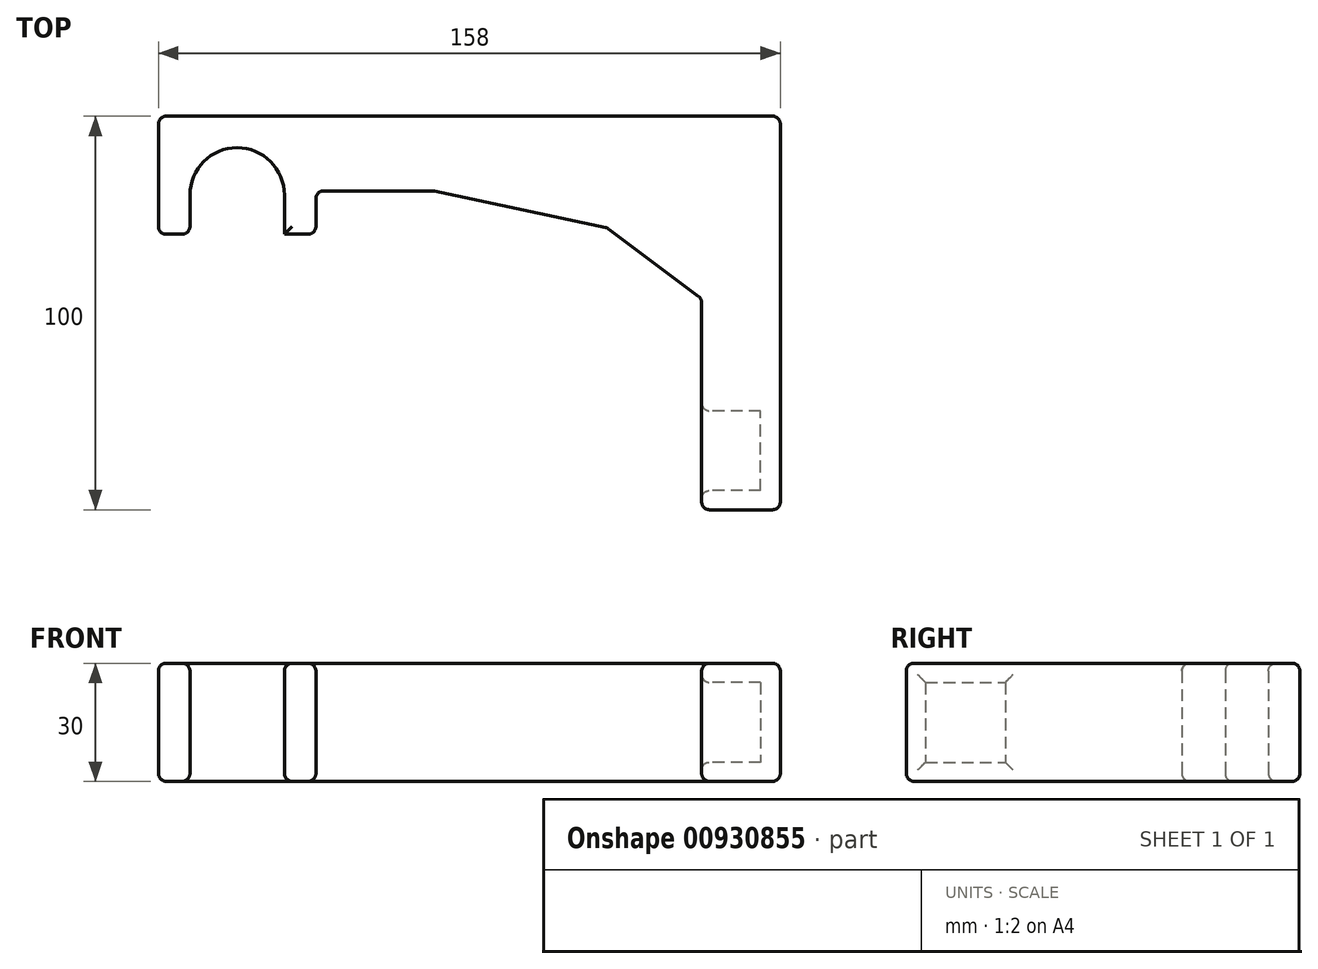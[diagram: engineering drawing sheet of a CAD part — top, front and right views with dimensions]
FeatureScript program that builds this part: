
annotation { "Feature Type Name" : "Feature", "Feature Type Description" : "" }
export const myFeature = defineFeature(function(context is Context, id is Id, definition is map)
    precondition{}
    {
        {
            var Q0;
            Q0=qCreatedBy(makeId("Top.planeOp"),FACE);
            var sketch = newSketch(context, id + "F0", { "sketchPlane" : qUnion([Q0])});
            skCircle(sketch, "E0", {"center": v(0, 5) * mm, "radius": 12 * mm});
            skLineSegment(sketch, "E1", {"start": v(-20, 25) * mm, "end": v(138, 25) * mm});
            skLineSegment(sketch, "E2", {"start": v(138, 25) * mm, "end": v(138, -15) * mm});
            skLineSegment(sketch, "E3", {"start": v(138, -15) * mm, "end": v(138, -75) * mm});
            skLineSegment(sketch, "E4", {"start": v(138, -75) * mm, "end": v(118, -75) * mm});
            skLineSegment(sketch, "E5", {"start": v(50, 5) * mm, "end": v(50, 6) * mm, "construction": true});
            skLineSegment(sketch, "E6", {"start": v(50, 6) * mm, "end": v(94.02, -3.36) * mm});
            skLineSegment(sketch, "E7", {"start": v(118, -75) * mm, "end": v(118, -21.38) * mm});
            skLineSegment(sketch, "E8", {"start": v(94.02, -3.36) * mm, "end": v(118, -21.38) * mm});
            skLineSegment(sketch, "E9", {"start": v(-12, 25) * mm, "end": v(-12, -5) * mm});
            skLineSegment(sketch, "E10.MirrorCS", {"start": v(12, 25) * mm, "end": v(12, -5) * mm});
            skLineSegment(sketch, "E11", {"start": v(-20, 25) * mm, "end": v(-20, -5) * mm});
            skLineSegment(sketch, "E12", {"start": v(-20, -5) * mm, "end": v(-12, -5) * mm});
            skLineSegment(sketch, "E13", {"start": v(12, -5) * mm, "end": v(20, -5) * mm});
            skLineSegment(sketch, "E14", {"start": v(50, 6) * mm, "end": v(20, 6) * mm});
            skLineSegment(sketch, "E15", {"start": v(20, 6) * mm, "end": v(20, -5) * mm});
            skLineSegment(sketch, "E16", {"start": v(0, 5) * mm, "end": v(118.79, 5) * mm, "construction": true});
            skSolve(sketch);
        }
        {
            var Q0;
            Q0=makeQuery(id+"F0.imprint","IMPRINT",FACE,{"disambiguationData":[TD([[makeQuery(id+"F0.imprint","IMPRINT",EDGE,{"derivedFrom":sQuery(id+"F0.wireOp",EDGE,"718Cw2XN-Loyv-s3oq-BlH3-nW312tGR8hBX.bottom")}),1.0]])]});
            var Q1;
            Q1=makeQuery(id+"F0.imprint","IMPRINT",FACE,{"disambiguationData":[TD([[makeQuery(id+"F0.imprint","IMPRINT",EDGE,{"derivedFrom":sQuery(id+"F0.wireOp",EDGE,"E1")}),-1.0]])]});
            var Q2;
            {var subQ3=sQuery(id+"F0.wireOp",EDGE,"zue7M12d-nwCh-ULH3-EO4g-m9Mkl6G7epCl");Q2=makeQuery(id+"F0.imprint","IMPRINT",FACE,{"disambiguationData":[TD([[makeQuery(id+"F0.imprint","IMPRINT",EDGE,{"derivedFrom":subQ3}),1.0]])]});}
            var Q3;
            {var subQ1=sQuery(id+"F0.wireOp",EDGE,"E3");Q3=makeQuery(id+"F0.imprint","IMPRINT",FACE,{"disambiguationData":[TD([[makeQuery(id+"F0.imprint","IMPRINT",EDGE,{"derivedFrom":subQ1}),-1.0]])]});}
            var Q4;
            {var subQ3=sQuery(id+"F0.wireOp",EDGE,"usQBu0dE-cOZz-AhfG-xYus-OKftIOVNqgJ2");Q4=makeQuery(id+"F0.imprint","IMPRINT",FACE,{"disambiguationData":[TD([[makeQuery(id+"F0.imprint","IMPRINT",EDGE,{"derivedFrom":subQ3}),-1.0]])]});}
            var Q5;
            {var subQ0=sQuery(id+"F0.wireOp",EDGE,"E11");Q5=makeQuery(id+"F0.imprint","IMPRINT",FACE,{"disambiguationData":[TD([[makeQuery(id+"F0.imprint","IMPRINT",EDGE,{"derivedFrom":subQ0}),1.0]])]});}
            extrude(context, id + "F1", {"entities" : qUnion([Q0, Q1, Q2, Q3, Q4, Q5]), "depth" : 30 * mm, "offsetDistance" : 25 * mm});
        }
        {
            var Q0;
            Q0=makeQuery(id+"F1.opExtrude","SWEPT_FACE",FACE,{"disambiguationData":[OSD([sQuery(id+"F0.wireOp",EDGE,"E7")])]});
            var sketch = newSketch(context, id + "F2", { "sketchPlane" : qUnion([Q0])});
            skLineSegment(sketch, "E17", {"start": v(75, 15) * mm, "end": v(21.38, 15) * mm, "construction": true});
            skPoint(sketch, "E18", {"position": v(60, 15) * mm});
            skLineSegment(sketch, "E19.bottom", {"start": v(70.12, 25.12) * mm, "end": v(49.87, 25.12) * mm});
            skLineSegment(sketch, "E19.top", {"start": v(70.12, 4.87) * mm, "end": v(49.87, 4.87) * mm});
            skLineSegment(sketch, "E19.left", {"start": v(70.12, 25.12) * mm, "end": v(70.12, 4.87) * mm});
            skLineSegment(sketch, "E19.right", {"start": v(49.87, 25.12) * mm, "end": v(49.87, 4.87) * mm});
            skSolve(sketch);
        }
        {
            var Q0;
            Q0=makeQuery(id+"F2.imprint","IMPRINT",FACE,{"disambiguationData":[TD([[makeQuery(id+"F2.imprint","IMPRINT",EDGE,{"derivedFrom":sQuery(id+"F2.wireOp",EDGE,"E19.bottom")}),1.0]])]});
            extrude(context, id + "F3", {"entities" : qUnion([Q0]), "operationType" : NewBodyOperationType.REMOVE, "oppositeDirection" : true, "depth" : 15 * mm, "offsetDistance" : 25 * mm});
        }
        {
            var Q0;
            Q0=makeQuery(id+"F1.opExtrude","SWEPT_FACE",FACE,{"disambiguationData":[OSD([sQuery(id+"F0.wireOp",EDGE,"E15")])]});
            var Q1;
            Q1=makeQuery(id+"F1.opExtrude","SWEPT_FACE",FACE,{"disambiguationData":[OSD([sQuery(id+"F0.wireOp",EDGE,"E14")])]});
            var Q2;
            Q2=makeQuery(id+"F1.opExtrude","SWEPT_FACE",FACE,{"disambiguationData":[OSD([sQuery(id+"F0.wireOp",EDGE,"E8")])]});
            var Q3;
            Q3=makeQuery(id+"F1.opExtrude","SWEPT_FACE",FACE,{"disambiguationData":[OSD([sQuery(id+"F0.wireOp",EDGE,"E7")])]});
            var Q4;
            Q4=makeQuery(id+"F1.opExtrude","SWEPT_FACE",FACE,{"disambiguationData":[OSD([sQuery(id+"F0.wireOp",EDGE,"E4")])]});
            var Q5;
            Q5=makeQuery(id+"F1.opExtrude","CAP_FACE",FACE,{"disambiguationData":[OSD([sQuery(id+"F0.wireOp",EDGE,"E0"),sQuery(id+"F0.wireOp",EDGE,"E1"),sQuery(id+"F0.wireOp",EDGE,"E2"),sQuery(id+"F0.wireOp",EDGE,"E3"),sQuery(id+"F0.wireOp",EDGE,"E4"),sQuery(id+"F0.wireOp",EDGE,"E6"),sQuery(id+"F0.wireOp",EDGE,"E7"),sQuery(id+"F0.wireOp",EDGE,"E8"),sQuery(id+"F0.wireOp",EDGE,"E9"),sQuery(id+"F0.wireOp",EDGE,"E10.MirrorCS"),sQuery(id+"F0.wireOp",EDGE,"E11"),sQuery(id+"F0.wireOp",EDGE,"E12"),sQuery(id+"F0.wireOp",EDGE,"E13"),sQuery(id+"F0.wireOp",EDGE,"E14"),sQuery(id+"F0.wireOp",EDGE,"E15")])],"isStart":false});
            var Q6;
            Q6=makeQuery(id+"F1.opExtrude","CAP_FACE",FACE,{"disambiguationData":[OSD([sQuery(id+"F0.wireOp",EDGE,"E0"),sQuery(id+"F0.wireOp",EDGE,"E1"),sQuery(id+"F0.wireOp",EDGE,"E2"),sQuery(id+"F0.wireOp",EDGE,"E3"),sQuery(id+"F0.wireOp",EDGE,"E4"),sQuery(id+"F0.wireOp",EDGE,"E6"),sQuery(id+"F0.wireOp",EDGE,"E7"),sQuery(id+"F0.wireOp",EDGE,"E8"),sQuery(id+"F0.wireOp",EDGE,"E9"),sQuery(id+"F0.wireOp",EDGE,"E10.MirrorCS"),sQuery(id+"F0.wireOp",EDGE,"E11"),sQuery(id+"F0.wireOp",EDGE,"E12"),sQuery(id+"F0.wireOp",EDGE,"E13"),sQuery(id+"F0.wireOp",EDGE,"E14"),sQuery(id+"F0.wireOp",EDGE,"E15")])],"isStart":true});
            var Q7;
            Q7=makeQuery(id+"F1.opExtrude","SWEPT_FACE",FACE,{"disambiguationData":[OSD([sQuery(id+"F0.wireOp",EDGE,"E12")])]});
            var Q8;
            Q8=makeQuery(id+"F1.opExtrude","SWEPT_FACE",FACE,{"disambiguationData":[OSD([sQuery(id+"F0.wireOp",EDGE,"E1")])]});
            fillet(context, id + "F4", {"entities" : qUnion([Q0, Q1, Q2, Q3, Q4, Q5, Q6, Q7, Q8]), "radius" : 2 * mm, "tangentPropagation" : true, "allowEdgeOverflow" : false});
        }
    });
